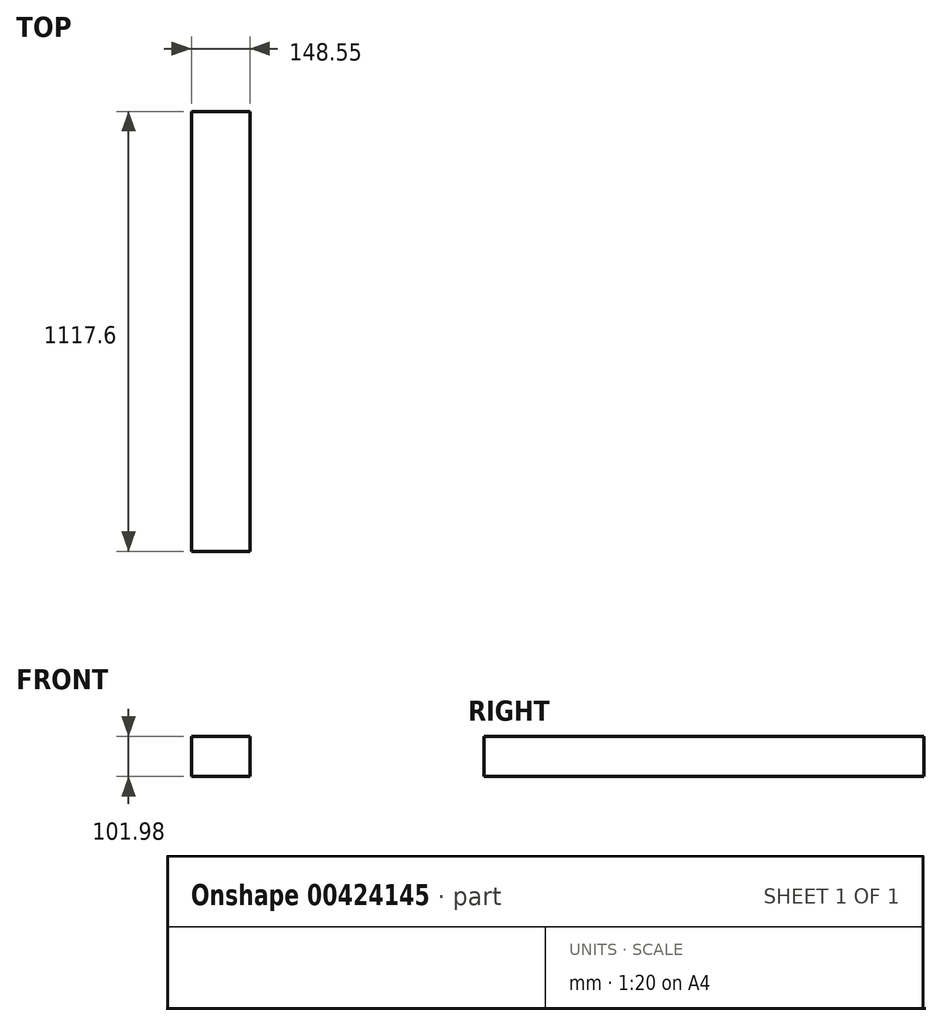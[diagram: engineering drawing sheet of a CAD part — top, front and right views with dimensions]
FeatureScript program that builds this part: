
annotation { "Feature Type Name" : "Feature", "Feature Type Description" : "" }
export const myFeature = defineFeature(function(context is Context, id is Id, definition is map)
    precondition{}
    {
        {
            var Q0;
            Q0=qCreatedBy(makeId("Front.planeOp"),FACE);
            var sketch = newSketch(context, id + "F0", { "sketchPlane" : qUnion([Q0])});
            skLineSegment(sketch, "E0.bottom", {"start": v(-72.84, 46.33) * mm, "end": v(75.71, 46.33) * mm});
            skLineSegment(sketch, "E0.top", {"start": v(-72.84, -55.65) * mm, "end": v(75.71, -55.65) * mm});
            skLineSegment(sketch, "E0.left", {"start": v(-72.84, 46.33) * mm, "end": v(-72.84, -55.65) * mm});
            skLineSegment(sketch, "E0.right", {"start": v(75.71, 46.33) * mm, "end": v(75.71, -55.65) * mm});
            skSolve(sketch);
        }
        {
            var Q0;
            Q0=makeQuery(id+"F0.imprint","IMPRINT",FACE,{"disambiguationData":[TD([[makeQuery(id+"F0.imprint","IMPRINT",EDGE,{"derivedFrom":sQuery(id+"F0.wireOp",EDGE,"E0.bottom")}),-1.0]])]});
            extrude(context, id + "F1", {"entities" : qUnion([Q0]), "depth" : 1117.6 * mm});
        }
    });
